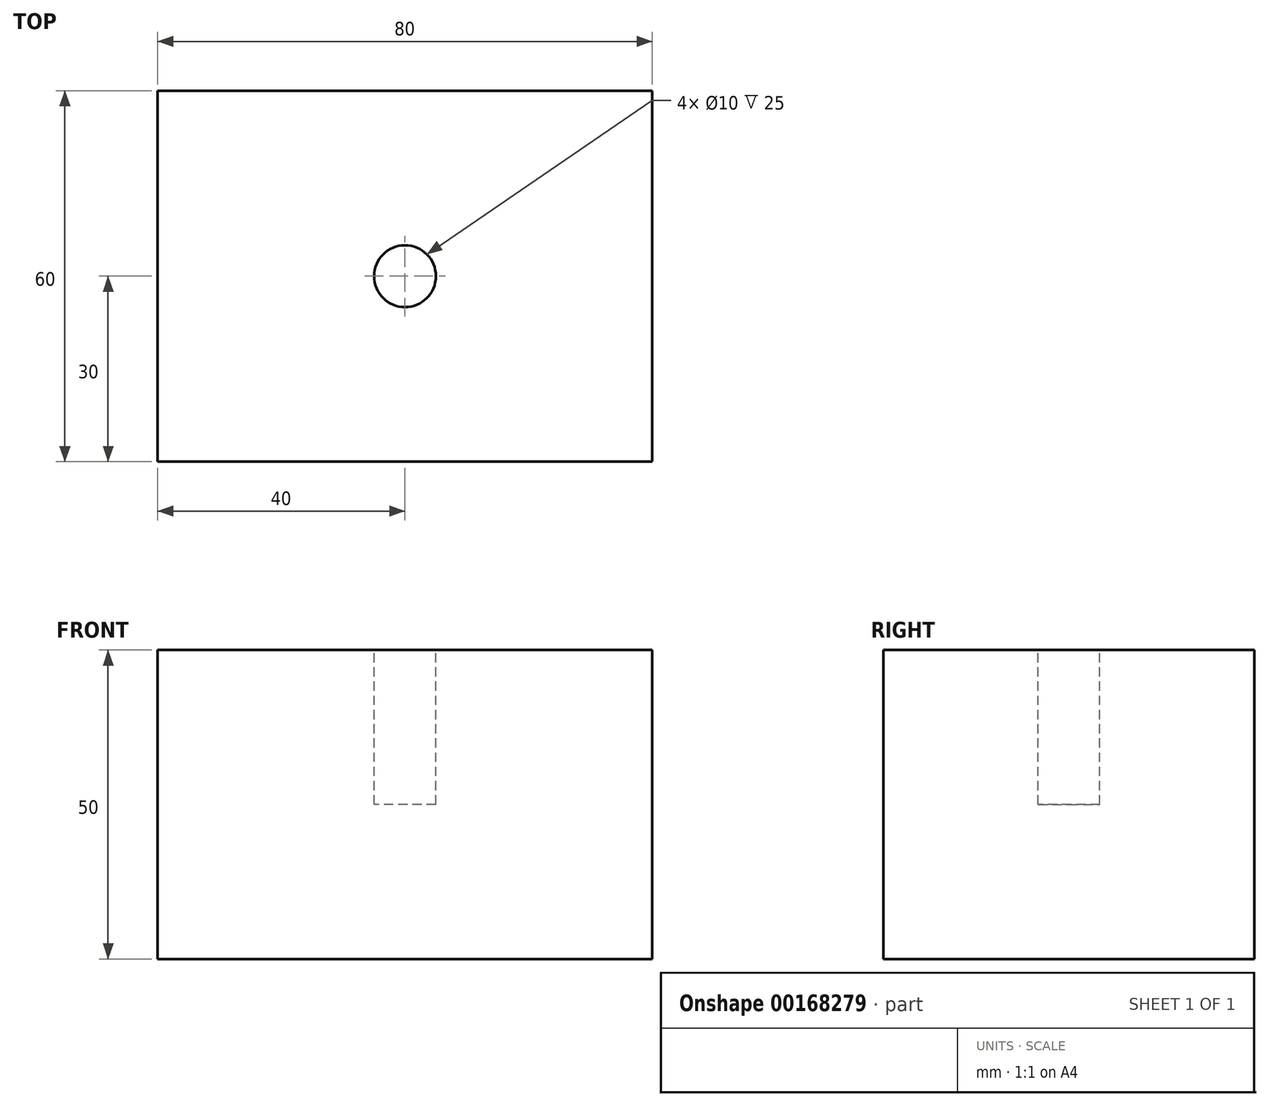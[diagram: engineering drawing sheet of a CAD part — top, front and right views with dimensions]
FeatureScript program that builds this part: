
annotation { "Feature Type Name" : "Feature", "Feature Type Description" : "" }
export const myFeature = defineFeature(function(context is Context, id is Id, definition is map)
    precondition{}
    {
        {
            var Q0;
            Q0=qCreatedBy(makeId("Top.planeOp"),FACE);
            var sketch = newSketch(context, id + "F0", { "sketchPlane" : qUnion([Q0])});
            skLineSegment(sketch, "E0.bottom", {"start": v(40, 30) * mm, "end": v(-40, 30) * mm});
            skLineSegment(sketch, "E0.top", {"start": v(40, -30) * mm, "end": v(-40, -30) * mm});
            skLineSegment(sketch, "E0.left", {"start": v(40, 30) * mm, "end": v(40, -30) * mm});
            skLineSegment(sketch, "E0.right", {"start": v(-40, 30) * mm, "end": v(-40, -30) * mm});
            skPoint(sketch, "E0.middle", {"position": v(0, 0) * mm});
            skSolve(sketch);
        }
        {
            var Q0;
            Q0=makeQuery(id+"F0.imprint","IMPRINT",FACE,{"disambiguationData":[TD([[makeQuery(id+"F0.imprint","IMPRINT",EDGE,{"derivedFrom":sQuery(id+"F0.wireOp",EDGE,"E0.bottom")}),1.0]])]});
            var Q1;
            Q1 = qSketchRegion(id + "F0", true);
            extrude(context, id + "F1", {"entities" : qUnion([Q0, Q1]), "depth" : 50 * mm});
        }
        {
            var Q0;
            Q0=makeQuery(id+"F1.opExtrude","CAP_FACE",FACE,{"disambiguationData":[OSD([sQuery(id+"F0.wireOp",EDGE,"E0.bottom"),sQuery(id+"F0.wireOp",EDGE,"E0.top"),sQuery(id+"F0.wireOp",EDGE,"E0.left"),sQuery(id+"F0.wireOp",EDGE,"E0.right")])],"isStart":false});
            var sketch = newSketch(context, id + "F2", { "sketchPlane" : qUnion([Q0])});
            skCircle(sketch, "E1", {"center": v(0, 0) * mm, "radius": 5 * mm});
            skSolve(sketch);
        }
        {
            var Q0;
            Q0 = qSketchRegion(id + "F2", true);
            extrude(context, id + "F3", {"entities" : qUnion([Q0]), "operationType" : NewBodyOperationType.REMOVE, "oppositeDirection" : true, "depth" : 25 * mm});
        }
    });
